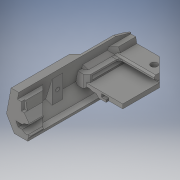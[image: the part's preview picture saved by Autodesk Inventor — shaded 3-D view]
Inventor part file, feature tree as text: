
AUTODESK INVENTOR PART (.ipt)
format: ipt  version: 2017 (Build 210142000, 142)  size: 382,464 bytes
history: native  units: in
note: dims shown in document units (in); Inventor stores cm internally (conversion verified against a paired STEP export)
features: extrude x5, sketch x5, other x2, chamfer x2, projected_geometry x1
ambient origin geometry x8: Origin, YZ Plane, XZ Plane, XY Plane, X Axis, Y Axis, Z Axis, Center Point
bodies: Solid1 (feature_tree)
feature tree (15):
  other  "05_cache cote carte SD+Ecran.STEP"
  extrude  "Extrusion1"  Depth=0.1969in TaperAngle=0.0deg
  extrude  "Extrusion2"  Depth=0.1969in TaperAngle=0.0deg
  extrude  "Extrusion3"  Depth=0.1969in TaperAngle=45.0deg
  extrude  "Extrusion4"  [1 undecoded]
  extrude  "Extrusion5"  [1 undecoded]
  chamfer  "Chamfer1"  [1 undecoded]
  chamfer  "Chamfer2"  [1 undecoded]
  sketch  "Sketch1"  dims[d0=0.1969in d1=0.0in d2=0.1969in d3=0.0in]
  sketch  "Sketch2"  dims[d4=0.1969in d5=0.0in d6=0.1969in d7=0.0in]
  sketch  "Sketch3"  dims[d8=0.1969in d9=0.0in d10=0.1969in d11=0.0787in d12=45.0deg]
  projected_geometry  "Projected Loop1"
  sketch  "Sketch4"  dims[d13=0.1969in d14=0.0787in d15=45.0deg]
  sketch  "Sketch5"
  other  "Enlèv. mat.-Extru.42"
note: 4 required parameter values undecoded (feature->parameter linkage not recoverable at this tier; creation-order binding heuristic only, values carry confidence <= 0.55)
